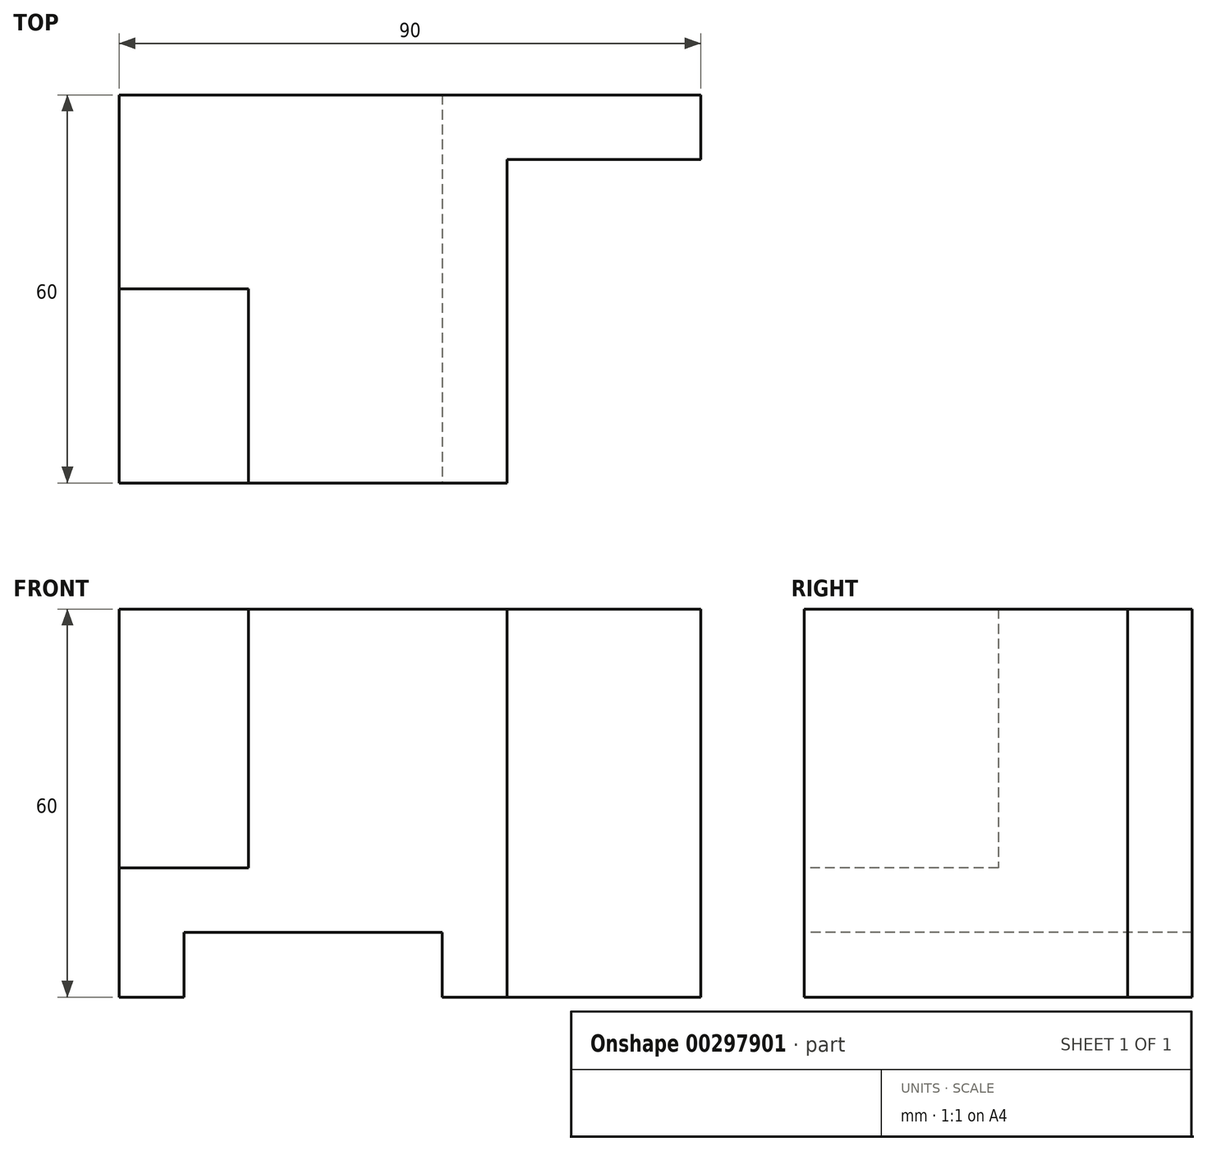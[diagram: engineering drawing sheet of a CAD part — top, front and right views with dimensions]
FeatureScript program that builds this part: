
annotation { "Feature Type Name" : "Feature", "Feature Type Description" : "" }
export const myFeature = defineFeature(function(context is Context, id is Id, definition is map)
    precondition{}
    {
        {
            var Q0;
            Q0=qCreatedBy(makeId("Front.planeOp"),FACE);
            var sketch = newSketch(context, id + "F0", { "sketchPlane" : qUnion([Q0])});
            skLineSegment(sketch, "E0.bottom", {"start": v(-39.46, 45.83) * mm, "end": v(50.54, 45.83) * mm});
            skLineSegment(sketch, "E0.top", {"start": v(-39.46, -14.17) * mm, "end": v(50.54, -14.17) * mm});
            skLineSegment(sketch, "E0.left", {"start": v(-39.46, 45.83) * mm, "end": v(-39.46, -14.17) * mm});
            skLineSegment(sketch, "E0.right", {"start": v(50.54, 45.83) * mm, "end": v(50.54, -14.17) * mm});
            skSolve(sketch);
        }
        {
            var Q0;
            Q0 = qSketchRegion(id + "F0", true);
            extrude(context, id + "F1", {"entities" : qUnion([Q0]), "depth" : 60 * mm});
        }
        {
            var Q0;
            Q0=makeQuery(id+"F1.opExtrude","SWEPT_FACE",FACE,{"disambiguationData":[OSD([sQuery(id+"F0.wireOp",EDGE,"E0.left")])]});
            var sketch = newSketch(context, id + "F2", { "sketchPlane" : qUnion([Q0])});
            skLineSegment(sketch, "E1.bottom", {"start": v(30, 45.83) * mm, "end": v(60, 45.83) * mm});
            skLineSegment(sketch, "E1.top", {"start": v(30, 5.83) * mm, "end": v(60, 5.83) * mm});
            skLineSegment(sketch, "E1.left", {"start": v(30, 45.83) * mm, "end": v(30, 5.83) * mm});
            skLineSegment(sketch, "E1.right", {"start": v(60, 45.83) * mm, "end": v(60, 5.83) * mm});
            skSolve(sketch);
        }
        {
            var Q0;
            Q0 = qSketchRegion(id + "F2", true);
            extrude(context, id + "F3", {"entities" : qUnion([Q0]), "operationType" : NewBodyOperationType.REMOVE, "oppositeDirection" : true, "depth" : 20 * mm});
        }
        {
            var Q0;
            Q0=makeQuery(id+"F1.opExtrude","SWEPT_FACE",FACE,{"disambiguationData":[OSD([sQuery(id+"F0.wireOp",EDGE,"E0.right")])]});
            var sketch = newSketch(context, id + "F4", { "sketchPlane" : qUnion([Q0])});
            skLineSegment(sketch, "E2.bottom", {"start": v(-10, 45.83) * mm, "end": v(-60, 45.83) * mm});
            skLineSegment(sketch, "E2.top", {"start": v(-10, -14.17) * mm, "end": v(-60, -14.17) * mm});
            skLineSegment(sketch, "E2.left", {"start": v(-10, 45.83) * mm, "end": v(-10, -14.17) * mm});
            skLineSegment(sketch, "E2.right", {"start": v(-60, 45.83) * mm, "end": v(-60, -14.17) * mm});
            skSolve(sketch);
        }
        {
            var Q0;
            Q0 = qSketchRegion(id + "F4", true);
            extrude(context, id + "F5", {"entities" : qUnion([Q0]), "operationType" : NewBodyOperationType.REMOVE, "oppositeDirection" : true, "depth" : 30 * mm});
        }
        {
            var Q0;
            Q0=makeQuery(id+"F1.opExtrude","CAP_FACE",FACE,{"disambiguationData":[OSD([sQuery(id+"F0.wireOp",EDGE,"E0.bottom"),sQuery(id+"F0.wireOp",EDGE,"E0.top"),sQuery(id+"F0.wireOp",EDGE,"E0.left"),sQuery(id+"F0.wireOp",EDGE,"E0.right")])],"isStart":false});
            var sketch = newSketch(context, id + "F6", { "sketchPlane" : qUnion([Q0])});
            skLineSegment(sketch, "E3.bottom", {"start": v(-29.46, -14.17) * mm, "end": v(10.54, -14.17) * mm});
            skLineSegment(sketch, "E3.top", {"start": v(-29.46, -4.17) * mm, "end": v(10.54, -4.17) * mm});
            skLineSegment(sketch, "E3.left", {"start": v(-29.46, -14.17) * mm, "end": v(-29.46, -4.17) * mm});
            skLineSegment(sketch, "E3.right", {"start": v(10.54, -14.17) * mm, "end": v(10.54, -4.17) * mm});
            skSolve(sketch);
        }
        {
            var Q0;
            Q0 = qSketchRegion(id + "F6", true);
            extrude(context, id + "F7", {"entities" : qUnion([Q0]), "operationType" : NewBodyOperationType.REMOVE, "endBound" : BoundingType.THROUGH_ALL, "oppositeDirection" : true, "depth" : 25 * mm});
        }
    });
